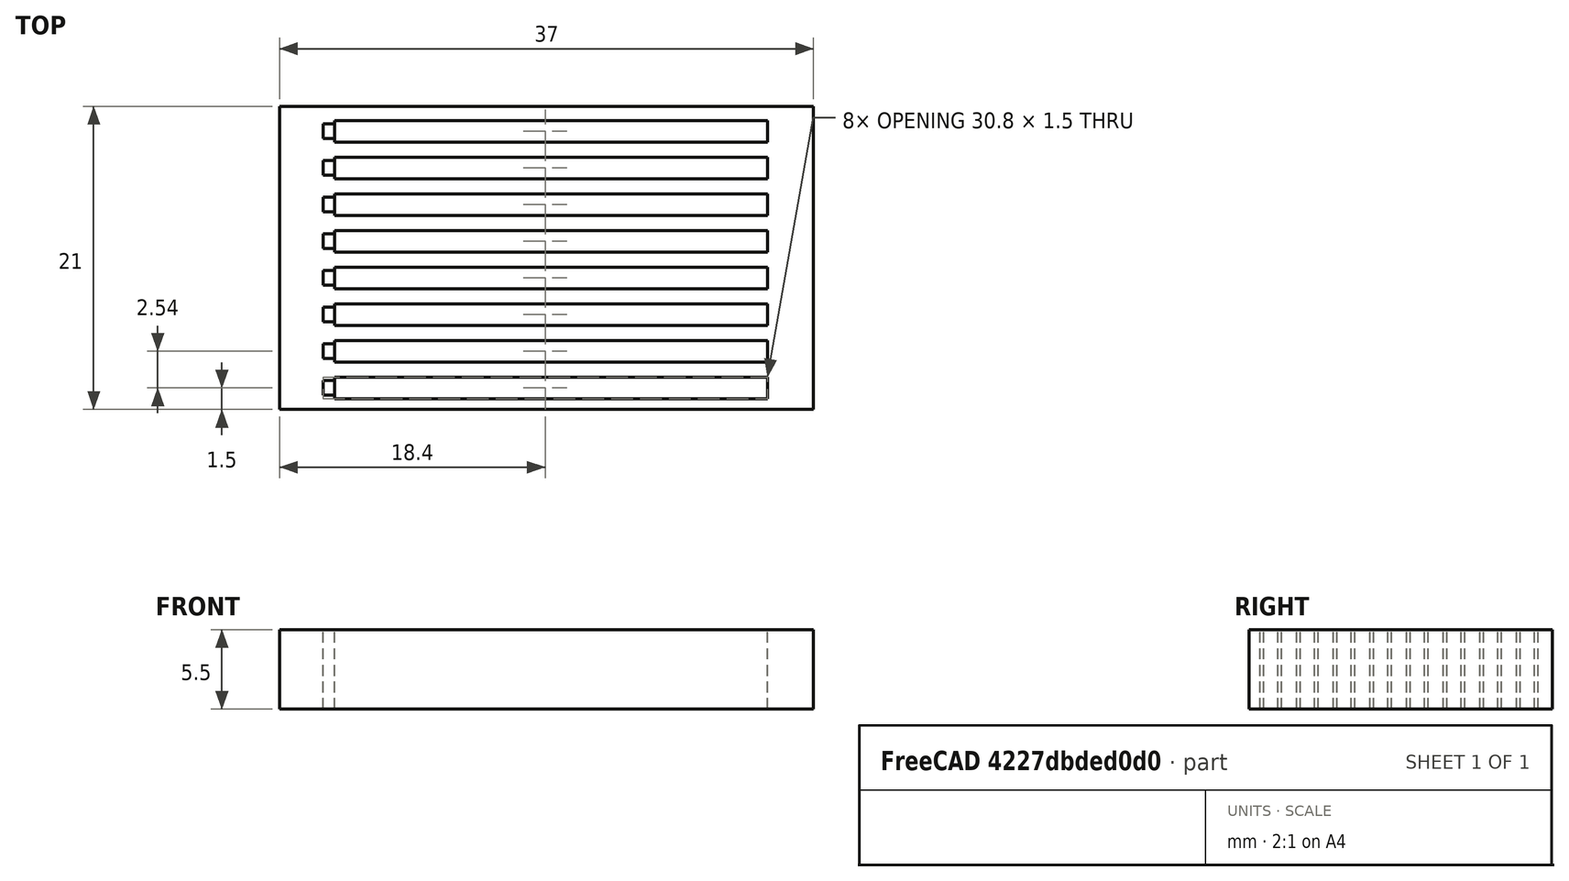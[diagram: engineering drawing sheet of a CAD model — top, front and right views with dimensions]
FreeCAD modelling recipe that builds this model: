
FCSTD DOCUMENT  (FreeCAD 0.17R13522 (Git))
Label: Test Piece V1 0.8
License: All rights reserved
LicenseURL: http://en.wikipedia.org/wiki/All_rights_reserved
objects: Part::Box×25, Part::MultiFuse×3, Part::Cut×2
note: 30 computed .brp shape members not serialized (recipe doc carries the construction recipe); baked Part::Feature solids carry a one-line shape summary decoded from their .brp

FEATURE [Part::Box] Box  label="Cube"
  AttacherType = Attacher::AttachEngine3D
  Height = 5.5
  Length = 37
  Width = 21
FEATURE [Part::Box] Box001  label="Cube001"
  AttacherType = Attacher::AttachEngine3D
  Height = 10
  Length = 0.8
  Placement = pos=(3,1,-3) rot=(0,0,1;0rad)
  Width = 1
FEATURE [Part::Box] Box002  label="Cube002"
  AttacherType = Attacher::AttachEngine3D
  Height = 10
  Length = 0.8
  Placement = pos=(3,3.54,-3) rot=(0,0,1;0rad)
  Width = 1
FEATURE [Part::Box] Box003  label="Cube003"
  AttacherType = Attacher::AttachEngine3D
  Height = 10
  Length = 0.8
  Placement = pos=(3,6.08,-3) rot=(0,0,1;0rad)
  Width = 1
FEATURE [Part::Box] Box004  label="Cube004"
  AttacherType = Attacher::AttachEngine3D
  Height = 10
  Length = 0.8
  Placement = pos=(3,8.62,-3) rot=(0,0,1;0rad)
  Width = 1
FEATURE [Part::Box] Box005  label="Cube005"
  AttacherType = Attacher::AttachEngine3D
  Height = 10
  Length = 0.8
  Placement = pos=(3,11.16,-3) rot=(0,0,1;0rad)
  Width = 1
FEATURE [Part::Box] Box006  label="Cube006"
  AttacherType = Attacher::AttachEngine3D
  Height = 10
  Length = 0.8
  Placement = pos=(3,13.7,-3) rot=(0,0,1;0rad)
  Width = 1
FEATURE [Part::Box] Box007  label="Cube007"
  AttacherType = Attacher::AttachEngine3D
  Height = 10
  Length = 0.8
  Placement = pos=(3,16.24,-3) rot=(0,0,1;0rad)
  Width = 1
FEATURE [Part::Box] Box008  label="Cube008"
  AttacherType = Attacher::AttachEngine3D
  Height = 10
  Length = 0.8
  Placement = pos=(3,18.78,-3) rot=(0,0,1;0rad)
  Width = 1
FEATURE [Part::Box] Box009  label="Cube009"
  AttacherType = Attacher::AttachEngine3D
  Height = 5.5
  Length = 30
  Placement = pos=(3.8,0.75,0) rot=(0,0,1;0rad)
  Width = 1.5
FEATURE [Part::Box] Box010  label="Cube010"
  AttacherType = Attacher::AttachEngine3D
  Height = 5.5
  Length = 30
  Placement = pos=(3.8,3.29,0) rot=(0,0,1;0rad)
  Width = 1.5
FEATURE [Part::Box] Box011  label="Cube011"
  AttacherType = Attacher::AttachEngine3D
  Height = 5.5
  Length = 30
  Placement = pos=(3.8,5.83,0) rot=(0,0,1;0rad)
  Width = 1.5
FEATURE [Part::Box] Box012  label="Cube012"
  AttacherType = Attacher::AttachEngine3D
  Height = 5.5
  Length = 30
  Placement = pos=(3.8,8.37,0) rot=(0,0,1;0rad)
  Width = 1.5
FEATURE [Part::Box] Box013  label="Cube013"
  AttacherType = Attacher::AttachEngine3D
  Height = 5.5
  Length = 30
  Placement = pos=(3.8,10.91,0) rot=(0,0,1;0rad)
  Width = 1.5
FEATURE [Part::Box] Box014  label="Cube014"
  AttacherType = Attacher::AttachEngine3D
  Height = 5.5
  Length = 30
  Placement = pos=(3.8,13.45,0) rot=(0,0,1;0rad)
  Width = 1.5
FEATURE [Part::Box] Box015  label="Cube015"
  AttacherType = Attacher::AttachEngine3D
  Height = 5.5
  Length = 30
  Placement = pos=(3.8,15.99,0) rot=(0,0,1;0rad)
  Width = 1.5
FEATURE [Part::Box] Box016  label="Cube016"
  AttacherType = Attacher::AttachEngine3D
  Height = 5.5
  Length = 30
  Placement = pos=(3.8,18.53,0) rot=(0,0,1;0rad)
  Width = 1.5
FEATURE [Part::MultiFuse] Fusion  label="Conducting Filament"
  Shapes = -> [Box009,Box010,Box011,Box012,Box013,Box014,Box015,Box016]
FEATURE [Part::MultiFuse] Fusion001
  Shapes = -> [Box001,Box002,Box003,Box004,Box005,Box006,Box007,Box008]
FEATURE [Part::Cut] Cut
  Base = -> Box
  Tool = -> Fusion001
FEATURE [Part::Box] Box017  label="Cube017"
  AttacherType = Attacher::AttachEngine3D
  Height = 5.5
  Length = 30
  Placement = pos=(3.8,0.75,0) rot=(0,0,1;0rad)
  Width = 1.5
FEATURE [Part::Box] Box018  label="Cube018"
  AttacherType = Attacher::AttachEngine3D
  Height = 5.5
  Length = 30
  Placement = pos=(3.8,10.91,0) rot=(0,0,1;0rad)
  Width = 1.5
FEATURE [Part::Box] Box019  label="Cube019"
  AttacherType = Attacher::AttachEngine3D
  Height = 5.5
  Length = 30
  Placement = pos=(3.8,3.29,0) rot=(0,0,1;0rad)
  Width = 1.5
FEATURE [Part::Box] Box020  label="Cube020"
  AttacherType = Attacher::AttachEngine3D
  Height = 5.5
  Length = 30
  Placement = pos=(3.8,5.83,0) rot=(0,0,1;0rad)
  Width = 1.5
FEATURE [Part::Box] Box021  label="Cube021"
  AttacherType = Attacher::AttachEngine3D
  Height = 5.5
  Length = 30
  Placement = pos=(3.8,18.53,0) rot=(0,0,1;0rad)
  Width = 1.5
FEATURE [Part::Box] Box022  label="Cube022"
  AttacherType = Attacher::AttachEngine3D
  Height = 5.5
  Length = 30
  Placement = pos=(3.8,15.99,0) rot=(0,0,1;0rad)
  Width = 1.5
FEATURE [Part::Box] Box023  label="Cube023"
  AttacherType = Attacher::AttachEngine3D
  Height = 5.5
  Length = 30
  Placement = pos=(3.8,8.37,0) rot=(0,0,1;0rad)
  Width = 1.5
FEATURE [Part::Box] Box024  label="Cube024"
  AttacherType = Attacher::AttachEngine3D
  Height = 5.5
  Length = 30
  Placement = pos=(3.8,13.45,0) rot=(0,0,1;0rad)
  Width = 1.5
FEATURE [Part::MultiFuse] Fusion002
  Shapes = -> [Box017,Box018,Box019,Box020,Box021,Box022,Box023,Box024]
FEATURE [Part::Cut] Cut001  label="Main body"
  Base = -> Cut
  Tool = -> Fusion002
